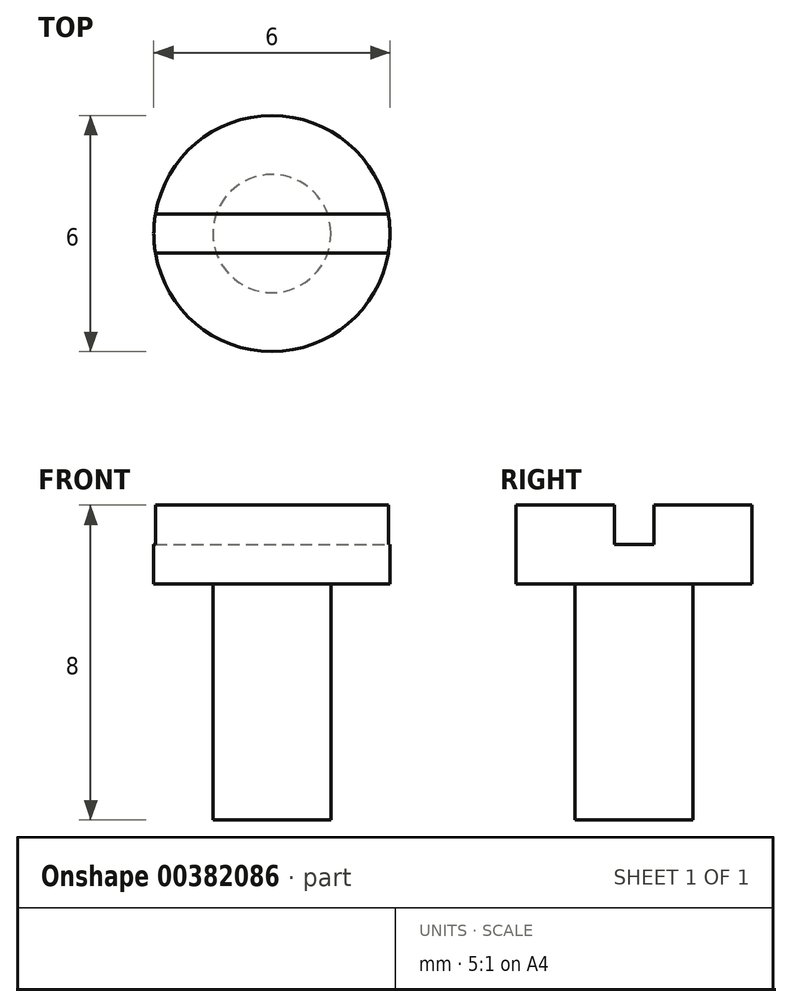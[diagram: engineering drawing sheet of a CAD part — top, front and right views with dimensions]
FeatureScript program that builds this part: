
annotation { "Feature Type Name" : "Feature", "Feature Type Description" : "" }
export const myFeature = defineFeature(function(context is Context, id is Id, definition is map)
    precondition{}
    {
        {
            var Q0;
            Q0=qCreatedBy(makeId("Top.planeOp"),FACE);
            var sketch = newSketch(context, id + "F0", { "sketchPlane" : qUnion([Q0])});
            skCircle(sketch, "E0", {"center": v(0, 0) * mm, "radius": 3 * mm});
            skLineSegment(sketch, "E1", {"start": v(-2.96, 0.5) * mm, "end": v(2.96, 0.5) * mm});
            skLineSegment(sketch, "E2.MirrorCS", {"start": v(-2.96, -0.5) * mm, "end": v(2.96, -0.5) * mm});
            skCircle(sketch, "E3", {"center": v(0, 0) * mm, "radius": 1.5 * mm});
            skSolve(sketch);
        }
        {
            var Q0;
            {var subQ0=sQuery(id+"F0.wireOp",EDGE,"E3");var subQ1=sQuery(id+"F0.wireOp",EDGE,"E1");var subQ2=makeQuery(id+"F0.imprint","INTERSECT",VERTEX,{"disambiguationData":[OD(0.0)],"derivedFrom":[subQ1,subQ0]});Q0=makeQuery(id+"F0.imprint","IMPRINT",FACE,{"disambiguationData":[TD([[makeQuery(id+"F0.imprint","IMPRINT",EDGE,{"disambiguationData":[TD([[subQ2,-1.0]])],"derivedFrom":subQ1}),1.0]])]});}
            var Q1;
            {var subQ0=sQuery(id+"F0.wireOp",EDGE,"E3");var subQ1=sQuery(id+"F0.wireOp",EDGE,"E1");var subQ2=makeQuery(id+"F0.imprint","INTERSECT",VERTEX,{"disambiguationData":[OD(0.0)],"derivedFrom":[subQ1,subQ0]});Q1=makeQuery(id+"F0.imprint","IMPRINT",FACE,{"disambiguationData":[TD([[makeQuery(id+"F0.imprint","IMPRINT",EDGE,{"disambiguationData":[TD([[subQ2,-1.0]])],"derivedFrom":subQ1}),-1.0]])]});}
            var Q2;
            {var subQ0=sQuery(id+"F0.wireOp",EDGE,"E3");var subQ1=sQuery(id+"F0.wireOp",EDGE,"E2.MirrorCS");var subQ2=makeQuery(id+"F0.imprint","INTERSECT",VERTEX,{"disambiguationData":[OD(0.0)],"derivedFrom":[subQ1,subQ0]});Q2=makeQuery(id+"F0.imprint","IMPRINT",FACE,{"disambiguationData":[TD([[makeQuery(id+"F0.imprint","IMPRINT",EDGE,{"disambiguationData":[TD([[subQ2,-1.0]])],"derivedFrom":subQ1}),-1.0]])]});}
            extrude(context, id + "F1", {"entities" : qUnion([Q0, Q1, Q2]), "oppositeDirection" : true, "depth" : 6 * mm});
        }
        {
            var Q0;
            Q0=makeQuery(id+"F0.imprint","IMPRINT",FACE,{"disambiguationData":[TD([[makeQuery(id+"F0.imprint","IMPRINT",EDGE,{"derivedFrom":sQuery(id+"F0.wireOp",EDGE,"95e27fa7-332e-4a81-bfd1-37d4185708e5.0")}),1.0]])]});
            var Q1;
            {var subQ0=sQuery(id+"F0.wireOp",EDGE,"E2.MirrorCS");Q1=makeQuery(id+"F0.imprint","IMPRINT",FACE,{"disambiguationData":[TD([[makeQuery(id+"F0.imprint","IMPRINT",EDGE,{"derivedFrom":subQ0}),-1.0]])]});}
            var Q2;
            {var subQ0=sQuery(id+"F0.wireOp",EDGE,"E1");Q2=makeQuery(id+"F0.imprint","IMPRINT",FACE,{"disambiguationData":[TD([[makeQuery(id+"F0.imprint","IMPRINT",EDGE,{"derivedFrom":subQ0}),1.0]])]});}
            var Q3;
            {var subQ0=sQuery(id+"F0.wireOp",EDGE,"E3");var subQ1=sQuery(id+"F0.wireOp",EDGE,"E1");var subQ2=makeQuery(id+"F0.imprint","INTERSECT",VERTEX,{"disambiguationData":[OD(0.0)],"derivedFrom":[subQ1,subQ0]});Q3=makeQuery(id+"F0.imprint","IMPRINT",FACE,{"disambiguationData":[TD([[makeQuery(id+"F0.imprint","IMPRINT",EDGE,{"disambiguationData":[TD([[subQ2,-1.0]])],"derivedFrom":subQ1}),1.0]])]});}
            var Q4;
            {var subQ0=sQuery(id+"F0.wireOp",EDGE,"E3");var subQ1=sQuery(id+"F0.wireOp",EDGE,"E2.MirrorCS");var subQ2=makeQuery(id+"F0.imprint","INTERSECT",VERTEX,{"disambiguationData":[OD(0.0)],"derivedFrom":[subQ1,subQ0]});Q4=makeQuery(id+"F0.imprint","IMPRINT",FACE,{"disambiguationData":[TD([[makeQuery(id+"F0.imprint","IMPRINT",EDGE,{"disambiguationData":[TD([[subQ2,-1.0]])],"derivedFrom":subQ1}),-1.0]])]});}
            extrude(context, id + "F2", {"entities" : qUnion([Q0, Q1, Q2, Q3, Q4]), "operationType" : NewBodyOperationType.ADD, "depth" : 2 * mm});
        }
        {
            var Q0;
            {var subQ0=sQuery(id+"F0.wireOp",EDGE,"E1");var subQ1=sQuery(id+"F0.wireOp",EDGE,"E0");var subQ2=makeQuery(id+"F0.imprint","INTERSECT",VERTEX,{"disambiguationData":[OD(0.0)],"derivedFrom":[subQ1,subQ0]});Q0=makeQuery(id+"F0.imprint","IMPRINT",FACE,{"disambiguationData":[TD([[makeQuery(id+"F0.imprint","IMPRINT",EDGE,{"disambiguationData":[TD([[subQ2,-1.0]])],"derivedFrom":subQ1}),1.0]])]});}
            var Q1;
            {var subQ0=sQuery(id+"F0.wireOp",EDGE,"E3");var subQ1=sQuery(id+"F0.wireOp",EDGE,"E1");var subQ2=makeQuery(id+"F0.imprint","INTERSECT",VERTEX,{"disambiguationData":[OD(0.0)],"derivedFrom":[subQ1,subQ0]});Q1=makeQuery(id+"F0.imprint","IMPRINT",FACE,{"disambiguationData":[TD([[makeQuery(id+"F0.imprint","IMPRINT",EDGE,{"disambiguationData":[TD([[subQ2,-1.0]])],"derivedFrom":subQ1}),-1.0]])]});}
            var Q2;
            {var subQ0=sQuery(id+"F0.wireOp",EDGE,"E1");var subQ1=sQuery(id+"F0.wireOp",EDGE,"E0");var subQ2=makeQuery(id+"F0.imprint","INTERSECT",VERTEX,{"disambiguationData":[OD(1.0)],"derivedFrom":[subQ1,subQ0]});Q2=makeQuery(id+"F0.imprint","IMPRINT",FACE,{"disambiguationData":[TD([[makeQuery(id+"F0.imprint","IMPRINT",EDGE,{"disambiguationData":[TD([[subQ2,1.0]])],"derivedFrom":subQ1}),1.0]])]});}
            extrude(context, id + "F3", {"entities" : qUnion([Q0, Q1, Q2]), "operationType" : NewBodyOperationType.ADD, "depth" : 1 * mm});
        }
    });
